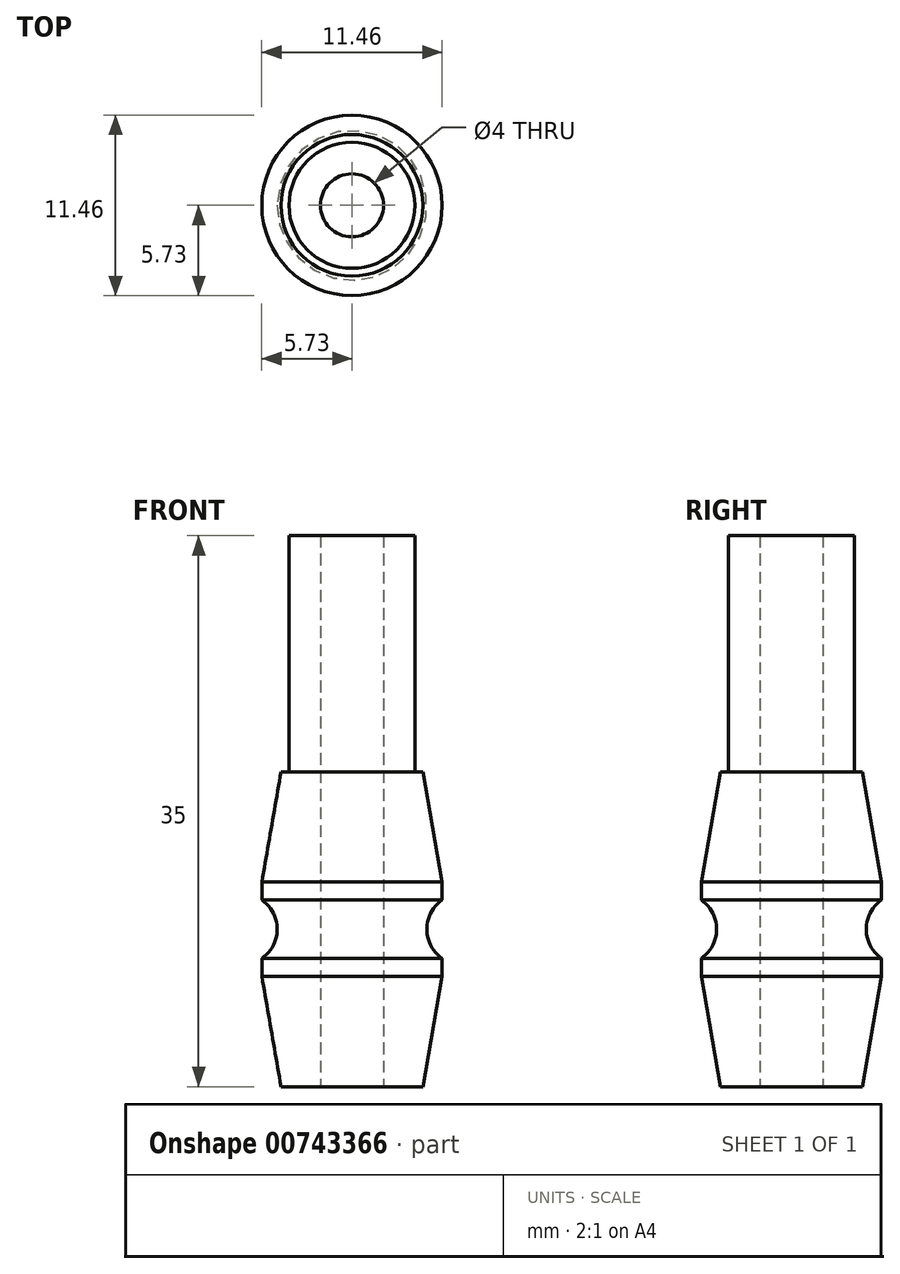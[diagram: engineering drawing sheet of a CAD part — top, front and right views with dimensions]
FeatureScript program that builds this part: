
annotation { "Feature Type Name" : "Feature", "Feature Type Description" : "" }
export const myFeature = defineFeature(function(context is Context, id is Id, definition is map)
    precondition{}
    {
        {
            var Q0;
            Q0=qCreatedBy(makeId("Front.planeOp"),FACE);
            var sketch = newSketch(context, id + "F0", { "sketchPlane" : qUnion([Q0])});
            skLineSegment(sketch, "E0", {"start": v(0, 0) * mm, "end": v(0, 17.76) * mm, "construction": true});
            skLineSegment(sketch, "E1", {"start": v(5.72, 7) * mm, "end": v(5.72, 8.15) * mm});
            skLineSegment(sketch, "E2", {"start": v(4, 20) * mm, "end": v(4.5, 20) * mm});
            skLineSegment(sketch, "E3", {"start": v(4.5, 20) * mm, "end": v(5.73, 13) * mm});
            skLineSegment(sketch, "E4", {"start": v(4.5, 0) * mm, "end": v(5.72, 7) * mm});
            skLineSegment(sketch, "E5", {"start": v(4, 20) * mm, "end": v(4, 35) * mm});
            skLineSegment(sketch, "E6", {"start": v(4, 35) * mm, "end": v(2, 35) * mm});
            skLineSegment(sketch, "E7", {"start": v(2, 35) * mm, "end": v(2, 0) * mm});
            skPoint(sketch, "E8.orphan", {"position": v(0, 35) * mm});
            skLineSegment(sketch, "E9", {"start": v(2, 0) * mm, "end": v(4.5, 0) * mm});
            skArc(sketch, "E10", {"start": v(5.73, 11.85) * mm, "mid": v(4.75, 10) * mm, "end": v(5.73, 8.15) * mm});
            skLineSegment(sketch, "E11.trimOffspring", {"start": v(5.72, 11.85) * mm, "end": v(5.72, 13) * mm});
            skSolve(sketch);
        }
        {
            var Q0;
            Q0 = qSketchRegion(id + "F0", true);
            var Q1;
            Q1=sQuery(id+"F0.wireOp",EDGE,"E0");
            revolve(context, id + "F1", {"surfaceOperationType" : NewSurfaceOperationType.NEW, "entities" : qUnion([Q0]), "axis" : qUnion([Q1]), "revolveType" : RevolveType.FULL});
        }
    });
